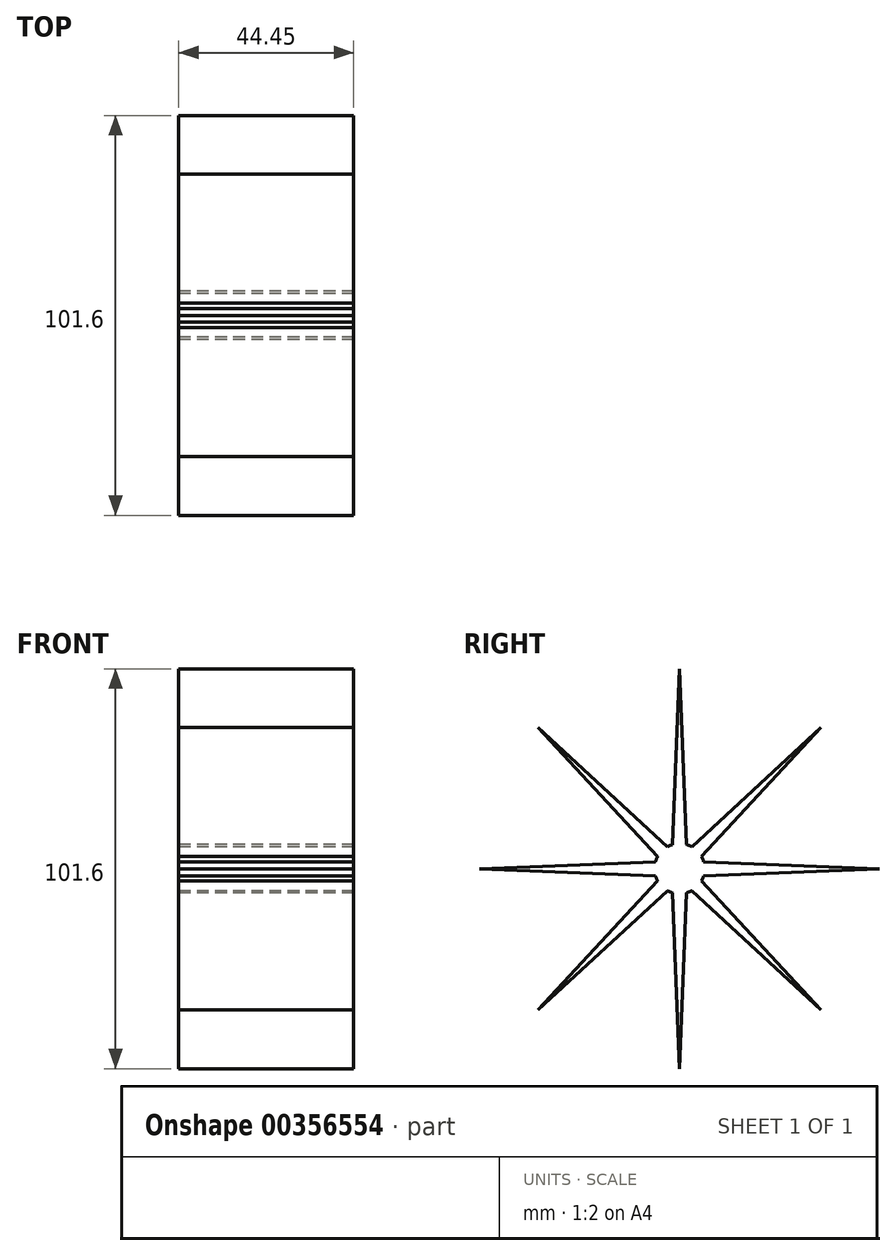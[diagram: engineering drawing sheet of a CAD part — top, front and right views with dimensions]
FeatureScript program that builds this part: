
annotation { "Feature Type Name" : "Feature", "Feature Type Description" : "" }
export const myFeature = defineFeature(function(context is Context, id is Id, definition is map)
    precondition{}
    {
        {
            var Q0;
            Q0=qCreatedBy(makeId("Right.planeOp"),FACE);
            var sketch = newSketch(context, id + "F0", { "sketchPlane" : qUnion([Q0])});
            skCircle(sketch, "E0", {"center": v(0, 0) * mm, "radius": 6.38 * mm});
            skLineSegment(sketch, "E1", {"start": v(0, 0) * mm, "end": v(-50.8, 0) * mm});
            skLineSegment(sketch, "E2", {"start": v(-50.8, 0) * mm, "end": v(0, 0) * mm});
            skLineSegment(sketch, "E3", {"start": v(0, 0) * mm, "end": v(0, 0) * mm});
            skLineSegment(sketch, "E4", {"start": v(0, 0) * mm, "end": v(-35.92, 35.92) * mm});
            skLineSegment(sketch, "E5", {"start": v(-35.92, 35.92) * mm, "end": v(0, 0) * mm});
            skLineSegment(sketch, "E6", {"start": v(0, 0) * mm, "end": v(0, 50.8) * mm});
            skLineSegment(sketch, "E7", {"start": v(0, 50.8) * mm, "end": v(0, 0) * mm});
            skLineSegment(sketch, "E8", {"start": v(0, 0) * mm, "end": v(35.92, 35.92) * mm});
            skLineSegment(sketch, "E9", {"start": v(35.92, 35.92) * mm, "end": v(0, 0) * mm});
            skLineSegment(sketch, "E10", {"start": v(0, 0) * mm, "end": v(50.8, 0) * mm});
            skLineSegment(sketch, "E11", {"start": v(50.8, 0) * mm, "end": v(0, 0) * mm});
            skLineSegment(sketch, "E12", {"start": v(0, 0) * mm, "end": v(35.92, -35.92) * mm});
            skLineSegment(sketch, "E13", {"start": v(35.92, -35.92) * mm, "end": v(0, 0) * mm});
            skLineSegment(sketch, "E14", {"start": v(0, 0) * mm, "end": v(0, -50.8) * mm});
            skLineSegment(sketch, "E15", {"start": v(0, -50.8) * mm, "end": v(0, 0) * mm});
            skLineSegment(sketch, "E16", {"start": v(0, 0) * mm, "end": v(-35.92, -35.92) * mm});
            skLineSegment(sketch, "E17", {"start": v(0, 50.8) * mm, "end": v(-1.94, 1.94) * mm});
            skLineSegment(sketch, "E18.MirrorCS", {"start": v(0, 50.8) * mm, "end": v(1.94, 1.94) * mm});
            skLineSegment(sketch, "E19.MirrorCS", {"start": v(50.8, 0) * mm, "end": v(1.94, 1.94) * mm});
            skLineSegment(sketch, "E20.MirrorCS", {"start": v(50.8, 0) * mm, "end": v(1.94, -1.94) * mm});
            skLineSegment(sketch, "E21.MirrorCS", {"start": v(0, -50.8) * mm, "end": v(1.94, -1.94) * mm});
            skLineSegment(sketch, "E22.MirrorCS", {"start": v(0, -50.8) * mm, "end": v(-1.94, -1.94) * mm});
            skLineSegment(sketch, "E23.MirrorCS", {"start": v(-50.8, 0) * mm, "end": v(-1.94, -1.94) * mm});
            skLineSegment(sketch, "E24.MirrorCS", {"start": v(-50.8, 0) * mm, "end": v(-1.94, 1.94) * mm});
            skLineSegment(sketch, "E25", {"start": v(35.92, 35.92) * mm, "end": v(1.84, 4.43) * mm});
            skLineSegment(sketch, "E26.MirrorCS", {"start": v(35.92, 35.92) * mm, "end": v(4.43, 1.84) * mm});
            skLineSegment(sketch, "E27.MirrorCS", {"start": v(35.92, -35.92) * mm, "end": v(4.43, -1.84) * mm});
            skLineSegment(sketch, "E28.MirrorCS", {"start": v(35.92, -35.92) * mm, "end": v(1.84, -4.43) * mm});
            skLineSegment(sketch, "E29.MirrorCS", {"start": v(-35.92, -35.92) * mm, "end": v(-1.84, -4.43) * mm});
            skLineSegment(sketch, "E30.MirrorCS", {"start": v(-35.92, -35.92) * mm, "end": v(-4.43, -1.84) * mm});
            skLineSegment(sketch, "E31.MirrorCS", {"start": v(-35.92, 35.92) * mm, "end": v(-1.84, 4.43) * mm});
            skLineSegment(sketch, "E32.MirrorCS", {"start": v(-35.92, 35.92) * mm, "end": v(-4.43, 1.84) * mm});
            skSolve(sketch);
        }
        {
            var Q0;
            Q0 = qSketchRegion(id + "F0", true);
            extrude(context, id + "F1", {"entities" : qUnion([Q0]), "depth" : 44.45 * mm});
        }
    });
